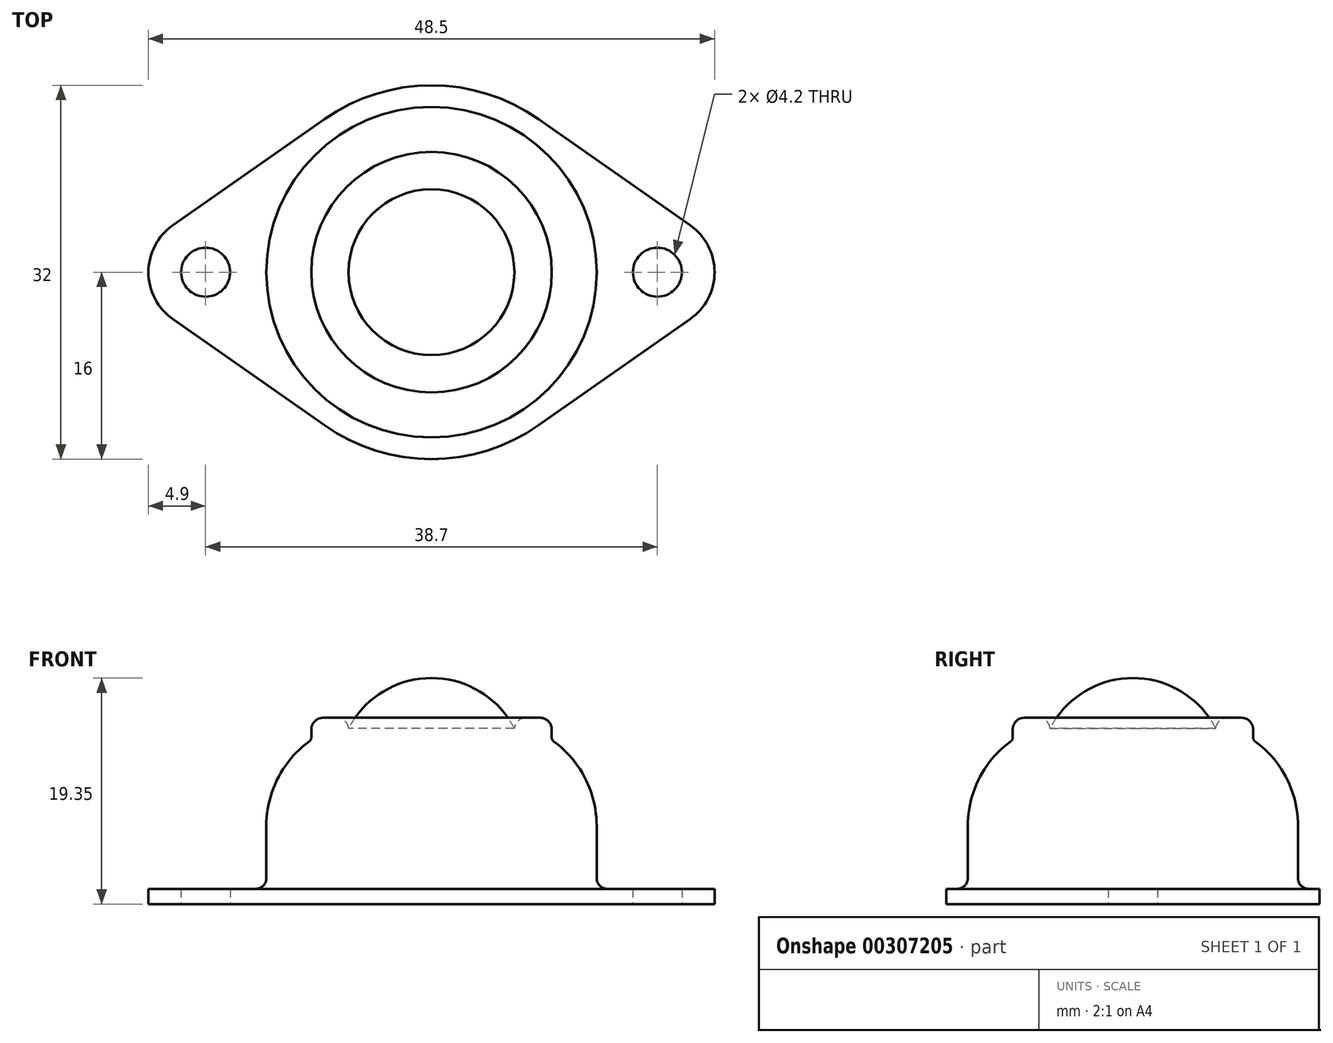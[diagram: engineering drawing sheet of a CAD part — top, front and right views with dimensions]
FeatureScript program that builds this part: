
annotation { "Feature Type Name" : "Feature", "Feature Type Description" : "" }
export const myFeature = defineFeature(function(context is Context, id is Id, definition is map)
    precondition{}
    {
        {
            var Q0;
            Q0=qCreatedBy(makeId("Top.planeOp"),FACE);
            var sketch = newSketch(context, id + "F0", { "sketchPlane" : qUnion([Q0])});
            skPoint(sketch, "E0.middle", {"position": v(0, 0) * mm});
            skCircle(sketch, "E1", {"center": v(19.35, 0) * mm, "radius": 2.1 * mm});
            skArc(sketch, "E2", {"start": v(22.16, -4.01) * mm, "mid": v(24.25, 0) * mm, "end": v(22.16, 4.01) * mm});
            skArc(sketch, "E3.MirrorC", {"start": v(-22.16, -4.01) * mm, "mid": v(-24.25, 0) * mm, "end": v(-22.16, 4.01) * mm});
            skCircle(sketch, "E4.MirrorC", {"center": v(-19.35, 0) * mm, "radius": 2.1 * mm});
            skCircle(sketch, "E5", {"center": v(0, 0) * mm, "radius": 14.15 * mm});
            skArc(sketch, "E6", {"start": v(9.18, 13.1) * mm, "mid": v(0, 16) * mm, "end": v(-9.18, 13.1) * mm});
            skLineSegment(sketch, "E7", {"start": v(-22.16, 4.01) * mm, "end": v(-9.18, 13.1) * mm});
            skLineSegment(sketch, "E8", {"start": v(9.18, 13.1) * mm, "end": v(22.16, 4.01) * mm});
            skLineSegment(sketch, "E9.MirrorCS", {"start": v(-22.16, -4.01) * mm, "end": v(-9.18, -13.1) * mm});
            skLineSegment(sketch, "E10.MirrorCS", {"start": v(9.18, -13.1) * mm, "end": v(22.16, -4.01) * mm});
            skArc(sketch, "E11.trimOffspring", {"start": v(-9.18, -13.1) * mm, "mid": v(0, -16) * mm, "end": v(9.18, -13.1) * mm});
            skCircle(sketch, "E12", {"center": v(0, 0) * mm, "radius": 10.3 * mm});
            skCircle(sketch, "E13", {"center": v(0, 0) * mm, "radius": 7.1 * mm});
            skSolve(sketch);
        }
        {
            var Q0;
            Q0=qSketchRegion(id+"F0",true);
            var Q1;
            Q1=makeQuery(id+"F0.imprint","IMPRINT",FACE,{"disambiguationData":[TD([[makeQuery(id+"F0.imprint","IMPRINT",EDGE,{"derivedFrom":sQuery(id+"F0.wireOp",EDGE,"E5")}),1.0]])]});
            var Q2;
            Q2=makeQuery(id+"F0.imprint","IMPRINT",FACE,{"disambiguationData":[TD([[makeQuery(id+"F0.imprint","IMPRINT",EDGE,{"derivedFrom":sQuery(id+"F0.wireOp",EDGE,"E12")}),1.0]])]});
            var Q3;
            Q3=makeQuery(id+"F0.imprint","IMPRINT",FACE,{"disambiguationData":[TD([[makeQuery(id+"F0.imprint","IMPRINT",EDGE,{"derivedFrom":sQuery(id+"F0.wireOp",EDGE,"E13")}),1.0]])]});
            extrude(context, id + "F1", {"entities" : qUnion([Q0, Q1, Q2, Q3]), "depth" : 1.3 * mm});
        }
        {
            var Q0;
            Q0=makeQuery(id+"F0.imprint","IMPRINT",FACE,{"disambiguationData":[TD([[makeQuery(id+"F0.imprint","IMPRINT",EDGE,{"derivedFrom":sQuery(id+"F0.wireOp",EDGE,"E12")}),1.0]])]});
            var Q1;
            Q1=makeQuery(id+"F0.imprint","IMPRINT",FACE,{"disambiguationData":[TD([[makeQuery(id+"F0.imprint","IMPRINT",EDGE,{"derivedFrom":sQuery(id+"F0.wireOp",EDGE,"E13")}),1.0]])]});
            var Q2;
            Q2=makeQuery(id+"F0.imprint","IMPRINT",FACE,{"disambiguationData":[TD([[makeQuery(id+"F0.imprint","IMPRINT",EDGE,{"derivedFrom":sQuery(id+"F0.wireOp",EDGE,"E5")}),1.0]])]});
            extrude(context, id + "F2", {"entities" : qUnion([Q0, Q1, Q2]), "operationType" : NewBodyOperationType.ADD, "depth" : 14.05 * mm});
        }
        {
            var Q0;
            Q0=makeQuery(id+"F0.imprint","IMPRINT",FACE,{"disambiguationData":[TD([[makeQuery(id+"F0.imprint","IMPRINT",EDGE,{"derivedFrom":sQuery(id+"F0.wireOp",EDGE,"E12")}),1.0]])]});
            extrude(context, id + "F3", {"entities" : qUnion([Q0]), "operationType" : NewBodyOperationType.ADD, "depth" : 15.95 * mm});
        }
        {
            var Q0;
            Q0=makeQuery(id+"F2.boolean.opBoolean","INTERSECT",EDGE,{"derivedFrom":[makeQuery(id+"F1.opExtrude","CAP_FACE",FACE,{"disambiguationData":[OSD([sQuery(id+"F0.wireOp",EDGE,"E1"),sQuery(id+"F0.wireOp",EDGE,"E2"),sQuery(id+"F0.wireOp",EDGE,"E3.MirrorC"),sQuery(id+"F0.wireOp",EDGE,"E4.MirrorC"),sQuery(id+"F0.wireOp",EDGE,"E6"),sQuery(id+"F0.wireOp",EDGE,"E7"),sQuery(id+"F0.wireOp",EDGE,"E8"),sQuery(id+"F0.wireOp",EDGE,"E9.MirrorCS"),sQuery(id+"F0.wireOp",EDGE,"E10.MirrorCS"),sQuery(id+"F0.wireOp",EDGE,"E11.trimOffspring")])],"isStart":false}),makeQuery(id+"F2.opExtrude","SWEPT_FACE",FACE,{"disambiguationData":[OSD([sQuery(id+"F0.wireOp",EDGE,"E5")])]})]});
            fillet(context, id + "F4", {"entities" : qUnion([Q0]), "radius" : 0.9 * mm, "tangentPropagation" : true, "allowEdgeOverflow" : false});
        }
        {
            var Q0;
            Q0=makeQuery(id+"F2.opExtrude","CAP_EDGE",EDGE,{"disambiguationData":[OSD([sQuery(id+"F0.wireOp",EDGE,"E5")])],"isStart":false});
            fillet(context, id + "F5", {"entities" : qUnion([Q0]), "radius" : 9 * mm, "tangentPropagation" : true, "allowEdgeOverflow" : false});
        }
        {
            var Q0;
            Q0=makeQuery(id+"F5.opFillet","BLEND_EDGE",EDGE,{"blendedFrom":[makeQuery(id+"F2.opExtrude","CAP_EDGE",EDGE,{"disambiguationData":[OSD([sQuery(id+"F0.wireOp",EDGE,"E5")])],"isStart":false}),makeQuery(id+"F3.opExtrude","SWEPT_FACE",FACE,{"disambiguationData":[OSD([sQuery(id+"F0.wireOp",EDGE,"E12")])]})],"blendedInto":[makeQuery(id+"F3.opExtrude","SWEPT_FACE",FACE,{"disambiguationData":[OSD([sQuery(id+"F0.wireOp",EDGE,"E12")])]})]});
            fillet(context, id + "F6", {"entities" : qUnion([Q0]), "radius" : 0.4 * mm, "tangentPropagation" : true, "allowEdgeOverflow" : false});
        }
        {
            var Q0;
            Q0=makeQuery(id+"F3.opExtrude","CAP_EDGE",EDGE,{"disambiguationData":[OSD([sQuery(id+"F0.wireOp",EDGE,"E12")])],"isStart":false});
            var Q1;
            Q1=makeQuery(id+"F3.opExtrude","CAP_EDGE",EDGE,{"disambiguationData":[OSD([sQuery(id+"F0.wireOp",EDGE,"E13")])],"isStart":false});
            fillet(context, id + "F7", {"entities" : qUnion([Q0, Q1]), "radius" : 1 * mm, "tangentPropagation" : true, "allowEdgeOverflow" : false});
        }
        {
            var Q0;
            Q0=makeQuery(id+"F3.opExtrude","CAP_FACE",FACE,{"disambiguationData":[OSD([sQuery(id+"F0.wireOp",EDGE,"E12"),sQuery(id+"F0.wireOp",EDGE,"E13")])],"isStart":false});
            cPlane(context, id + "F8", {"entities" : qUnion([Q0]), "cplaneType" : CPlaneType.OFFSET, "offset" : 4.6 * mm, "oppositeDirection" : true, "width" : 150 * mm, "height" : 150 * mm});
        }
        {
            var Q0;
            Q0=qCreatedBy(id+"F8.planeOp",FACE);
            var sketch = newSketch(context, id + "F9", { "sketchPlane" : qUnion([Q0])});
            skPoint(sketch, "E14.0", {"position": v(0, 0) * mm});
            skArc(sketch, "E15", {"start": v(0, 8) * mm, "mid": v(-8, 0) * mm, "end": v(0, -8) * mm});
            skPoint(sketch, "E16", {"position": v(0, -9.77) * mm});
            skLineSegment(sketch, "E17", {"start": v(0, -9.77) * mm, "end": v(0, 9.64) * mm});
            skSolve(sketch);
        }
        {
            var Q0;
            {var subQ0=sQuery(id+"F9.wireOp",EDGE,"E15");Q0=makeQuery(id+"F9.imprint","IMPRINT",FACE,{"disambiguationData":[TD([[makeQuery(id+"F9.imprint","IMPRINT",EDGE,{"derivedFrom":subQ0}),1.0]])]});}
            var Q1;
            Q1=sQuery(id+"F9.wireOp",EDGE,"E15");
            var Q2;
            Q2=sQuery(id+"F9.wireOp",EDGE,"E17");
            revolve(context, id + "F10", {"operationType" : NewBodyOperationType.ADD, "entities" : qUnion([Q0]), "surfaceEntities" : qUnion([Q1]), "axis" : qUnion([Q2]), "revolveType" : RevolveType.FULL});
        }
    });
